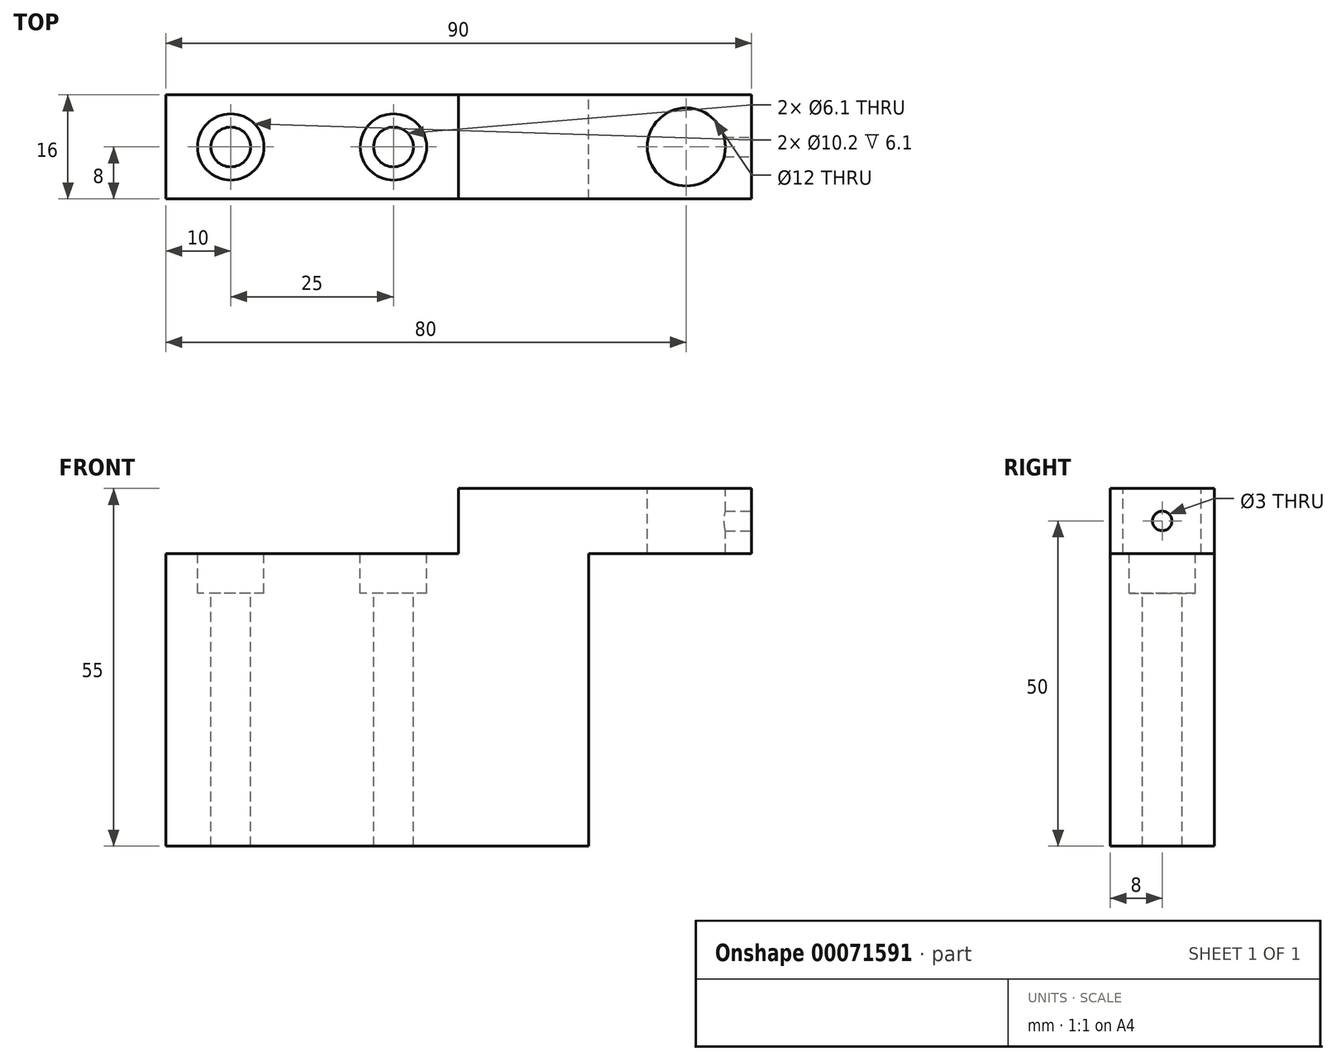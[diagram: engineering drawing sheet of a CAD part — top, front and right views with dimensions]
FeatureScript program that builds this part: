
annotation { "Feature Type Name" : "Feature", "Feature Type Description" : "" }
export const myFeature = defineFeature(function(context is Context, id is Id, definition is map)
    precondition{}
    {
        {
            var Q0;
            Q0=qCreatedBy(makeId("Front.planeOp"),FACE);
            cPlane(context, id + "F0", {"entities" : qUnion([Q0]), "cplaneType" : CPlaneType.OFFSET, "offset" : 50 * mm, "oppositeDirection" : true, "width" : 150 * mm, "height" : 150 * mm});
        }
        {
            var Q0;
            Q0=qCreatedBy(id+"F0.planeOp",FACE);
            var sketch = newSketch(context, id + "F1", { "sketchPlane" : qUnion([Q0])});
            skLineSegment(sketch, "E0", {"start": v(0, 10) * mm, "end": v(0, 55) * mm});
            skLineSegment(sketch, "E1", {"start": v(0, 55) * mm, "end": v(45, 55) * mm});
            skLineSegment(sketch, "E2", {"start": v(45, 55) * mm, "end": v(45, 65) * mm});
            skLineSegment(sketch, "E3", {"start": v(45, 65) * mm, "end": v(90, 65) * mm});
            skLineSegment(sketch, "E4", {"start": v(90, 65) * mm, "end": v(90, 55) * mm});
            skLineSegment(sketch, "E5", {"start": v(90, 55) * mm, "end": v(65, 55) * mm});
            skLineSegment(sketch, "E6", {"start": v(65, 55) * mm, "end": v(65, 10) * mm});
            skLineSegment(sketch, "E7", {"start": v(65, 10) * mm, "end": v(0, 10) * mm});
            skSolve(sketch);
        }
        {
            var Q0;
            Q0=qSketchRegion(id+"F1",true);
            extrude(context, id + "F2", {"entities" : qUnion([Q0]), "endBound" : BoundingType.SYMMETRIC, "depth" : 16 * mm});
        }
        {
            var Q0;
            Q0=makeQuery(id+"F2.opExtrude","SWEPT_FACE",FACE,{"disambiguationData":[OSD([sQuery(id+"F1.wireOp",EDGE,"E1")])]});
            var sketch = newSketch(context, id + "F3", { "sketchPlane" : qUnion([Q0])});
            skCircle(sketch, "E8", {"center": v(10, 50) * mm, "radius": 3.05 * mm});
            skPoint(sketch, "E8.centerSnap0", {"position": v(0, 50) * mm});
            skCircle(sketch, "E9", {"center": v(35, 50) * mm, "radius": 3.05 * mm});
            skSolve(sketch);
        }
        {
            var Q0;
            Q0=qSketchRegion(id+"F3",true);
            extrude(context, id + "F4", {"entities" : qUnion([Q0]), "operationType" : NewBodyOperationType.REMOVE, "endBound" : BoundingType.UP_TO_NEXT, "oppositeDirection" : true, "depth" : 25 * mm});
        }
        {
            var Q0;
            Q0=makeQuery(id+"F2.opExtrude","SWEPT_FACE",FACE,{"disambiguationData":[OSD([sQuery(id+"F1.wireOp",EDGE,"E1")])]});
            var sketch = newSketch(context, id + "F5", { "sketchPlane" : qUnion([Q0])});
            skCircle(sketch, "E10", {"center": v(10, 50) * mm, "radius": 5.1 * mm});
            skCircle(sketch, "E11", {"center": v(35, 50) * mm, "radius": 5.1 * mm});
            skSolve(sketch);
        }
        {
            var Q0;
            Q0=qSketchRegion(id+"F5",true);
            extrude(context, id + "F6", {"entities" : qUnion([Q0]), "operationType" : NewBodyOperationType.REMOVE, "oppositeDirection" : true, "depth" : 6.1 * mm});
        }
        {
            var Q0;
            Q0=makeQuery(id+"F2.opExtrude","SWEPT_FACE",FACE,{"disambiguationData":[OSD([sQuery(id+"F1.wireOp",EDGE,"E3")])]});
            var sketch = newSketch(context, id + "F7", { "sketchPlane" : qUnion([Q0])});
            skCircle(sketch, "E12", {"center": v(80, 50) * mm, "radius": 6 * mm});
            skPoint(sketch, "E12.centerSnap0", {"position": v(90, 50) * mm});
            skSolve(sketch);
        }
        {
            var Q0;
            Q0=qSketchRegion(id+"F7",true);
            extrude(context, id + "F8", {"entities" : qUnion([Q0]), "operationType" : NewBodyOperationType.REMOVE, "endBound" : BoundingType.UP_TO_NEXT, "oppositeDirection" : true, "depth" : 25 * mm});
        }
        {
            var Q0;
            Q0=makeQuery(id+"F2.opExtrude","SWEPT_FACE",FACE,{"disambiguationData":[OSD([sQuery(id+"F1.wireOp",EDGE,"E4")])]});
            var sketch = newSketch(context, id + "F9", { "sketchPlane" : qUnion([Q0])});
            skCircle(sketch, "E13", {"center": v(50, 60) * mm, "radius": 1.5 * mm});
            skPoint(sketch, "E13.centerSnap0", {"position": v(42, 60) * mm});
            skPoint(sketch, "E13.centerSnap1", {"position": v(50, 65) * mm});
            skSolve(sketch);
        }
        {
            var Q0;
            Q0=qSketchRegion(id+"F9",true);
            extrude(context, id + "F10", {"entities" : qUnion([Q0]), "operationType" : NewBodyOperationType.REMOVE, "endBound" : BoundingType.UP_TO_NEXT, "oppositeDirection" : true, "depth" : 25 * mm});
        }
    });
